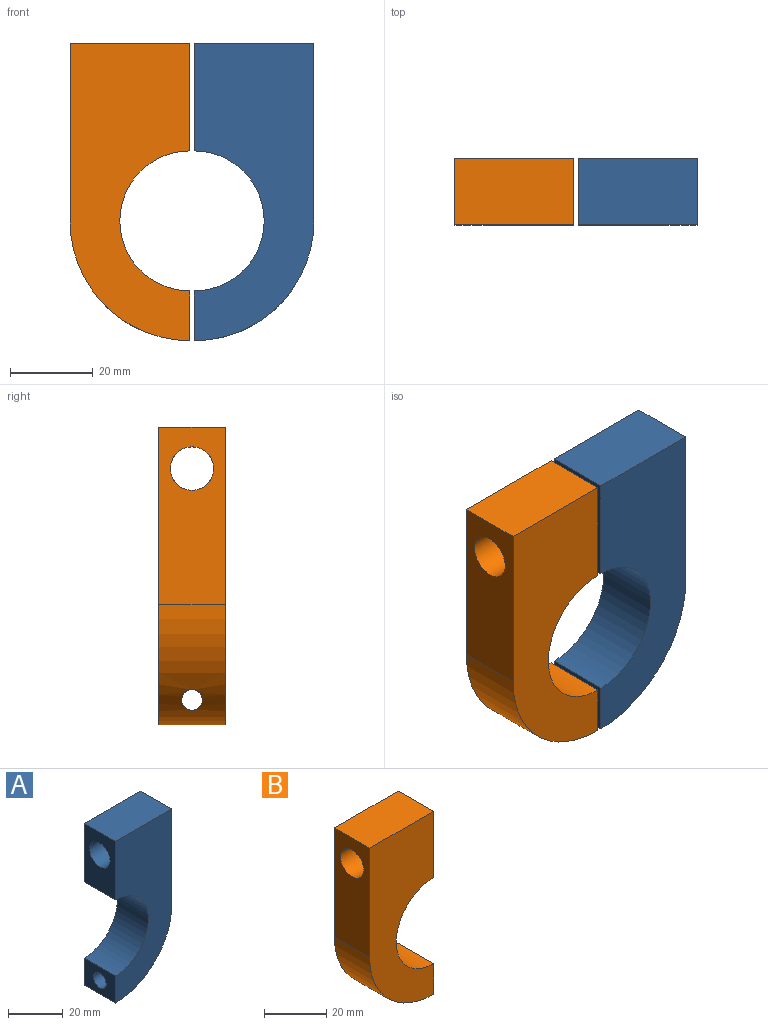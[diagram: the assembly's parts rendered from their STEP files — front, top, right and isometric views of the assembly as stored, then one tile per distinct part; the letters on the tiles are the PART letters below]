
ASSEMBLY  parts=2 mates=1
PART A: 12 faces, bbox 29x16x72 mm
  f0: plane 26.05x16mm, normal (-1,0,0), area 330.2mm2, adj f1,f5,f6,f7,f8
  f1: cylinder r=16.95mm len=33.9mm, axis (0,1,0), area 852mm2, adj f0,f2,f6,f7
  f2: plane 16x12.05mm, normal (-1,0,0), area 159.6mm2, adj f1,f3,f6,f7,f9
  f3: cylinder r=29mm len=29mm, axis (0,1,0), area 539.6mm2, adj f2,f4,f6,f7,f10,f11
  f4: plane 43x16mm, normal (1,0,0), area 601.4mm2, adj f3,f5,f6,f7,f8
  f5: plane 29x16mm, normal (0,0,1), area 464mm2, adj f0,f4,f6,f7
  f6: plane 72x29mm, normal (0,-1,0), area 1456.2mm2, adj f0,f1,f2,f3,f4,f5
  f7: plane 72x29mm, normal (0,1,0), area 1456.2mm2, adj f0,f1,f2,f3,f4,f5
  f8: cylinder r=5.25mm len=29mm, axis (-1,0,0), area 956.6mm2, adj f0,f4
  f9: cylinder r=3.25mm len=6.5mm, axis (-1,0,0), area 122.5mm2, adj f2,f11
  f10: cylinder r=5.75mm len=17.31mm, axis (-1,0,0), area 364.5mm2, adj f3,f11
  f11: plane 11.5x11.12mm, normal (1,0,0), area 69.6mm2, adj f3,f9,f10
PART B: 10 faces, bbox 29x16x72 mm
  f0: cylinder r=29mm len=29mm, axis (0,1,0), area 696.1mm2, adj f4,f5,f6,f7,f9
  f1: cylinder r=16.95mm len=33.9mm, axis (0,1,0), area 852mm2, adj f2,f5,f6,f7
  f2: plane 26.05x16mm, normal (1,0,0), area 330.2mm2, adj f1,f3,f6,f7,f8
  f3: plane 29x16mm, normal (0,0,1), area 464mm2, adj f2,f4,f6,f7
  f4: plane 43x16mm, normal (-1,0,0), area 601.4mm2, adj f0,f3,f6,f7,f8
  f5: plane 16x12.05mm, normal (1,0,0), area 173.2mm2, adj f0,f1,f6,f7,f9
  f6: plane 72x29mm, normal (0,-1,0), area 1456.2mm2, adj f0,f1,f2,f3,f4,f5
  f7: plane 72x29mm, normal (0,1,0), area 1456.2mm2, adj f0,f1,f2,f3,f4,f5
  f8: cylinder r=5.25mm len=29mm, axis (1,0,0), area 956.6mm2, adj f2,f4
  f9: cylinder r=2.5mm len=20.51mm, axis (1,0,0), area 273.6mm2, adj f0,f5
PLACE A t=(0,-8.28,-0.63)mm
PLACE B t=(-1.05,-8.28,-0.63)mm
MATE cylindrical B.f8 <-> A.f8  axis (1,0,0) through (-1.05,-8.28,32.37)mm
